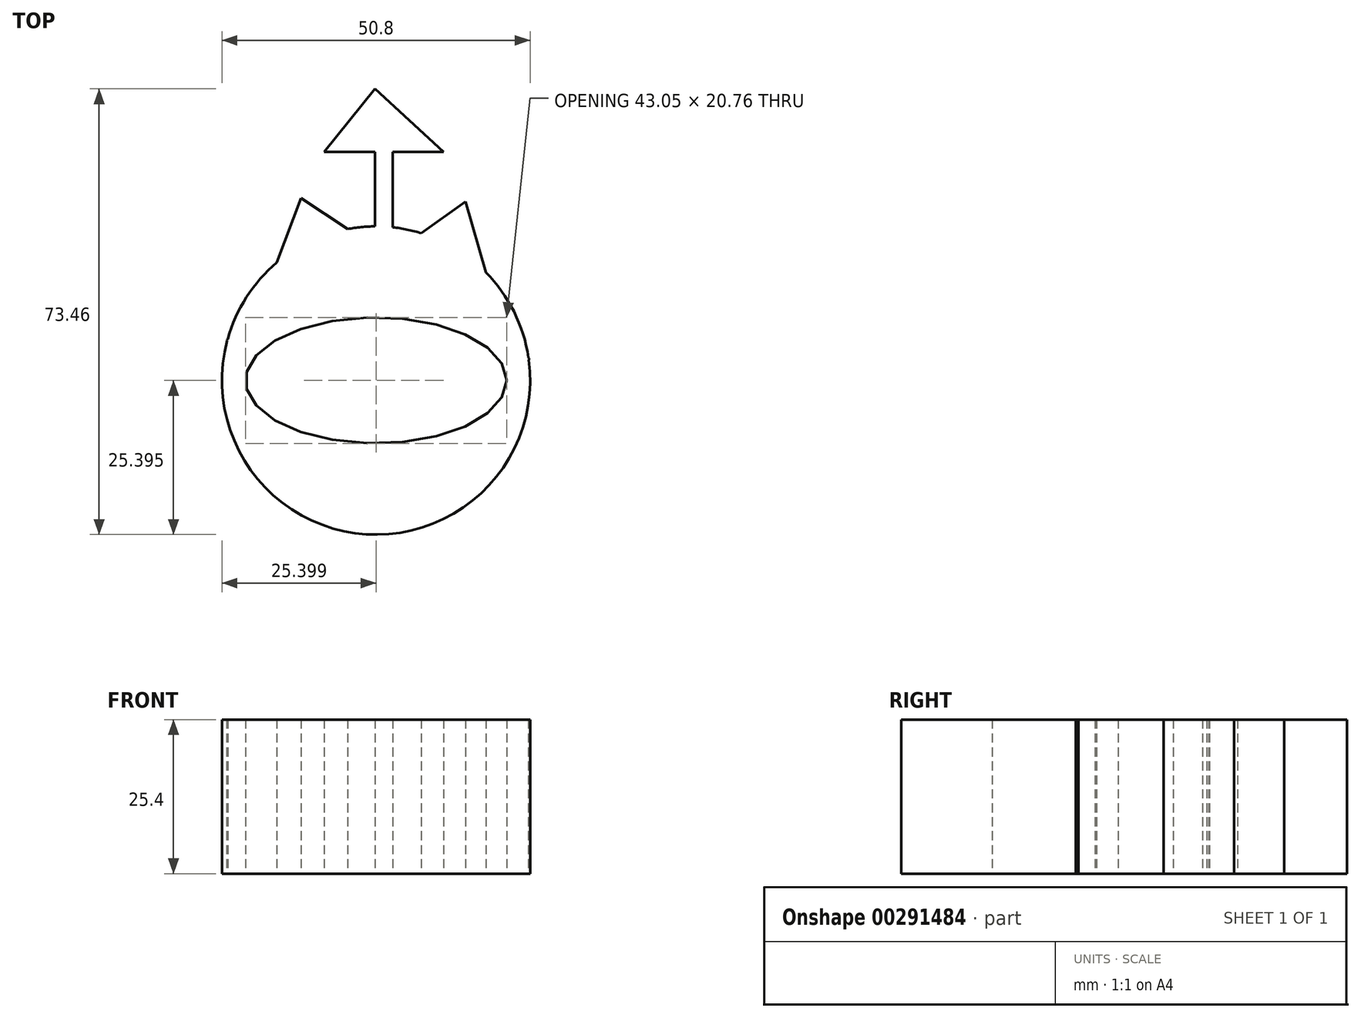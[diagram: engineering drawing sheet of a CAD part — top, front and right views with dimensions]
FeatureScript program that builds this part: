
annotation { "Feature Type Name" : "Feature", "Feature Type Description" : "" }
export const myFeature = defineFeature(function(context is Context, id is Id, definition is map)
    precondition{}
    {
        {
            var Q0;
            Q0=qCreatedBy(makeId("Top.planeOp"),FACE);
            var sketch = newSketch(context, id + "F0", { "sketchPlane" : qUnion([Q0])});
            skArc(sketch, "E0", {"start": v(-48.95, 34.93) * mm, "mid": v(-33.79, -9.89) * mm, "end": v(-14.51, 33.32) * mm});
            skLineSegment(sketch, "E1", {"start": v(-48.95, 34.93) * mm, "end": v(-44.98, 45.53) * mm});
            skLineSegment(sketch, "E2", {"start": v(-37.3, 40.45) * mm, "end": v(-44.98, 45.53) * mm});
            skLineSegment(sketch, "E3", {"start": v(-25.13, 39.76) * mm, "end": v(-17.83, 44.96) * mm});
            skLineSegment(sketch, "E4", {"start": v(-17.83, 44.96) * mm, "end": v(-14.51, 33.32) * mm});
            skLineSegment(sketch, "E5", {"start": v(-32.76, 40.88) * mm, "end": v(-32.76, 53.19) * mm});
            skPoint(sketch, "E6.endSnap0", {"position": v(-21.48, 42.36) * mm});
            skArc(sketch, "E7.trimOffspring", {"start": v(-25.13, 39.76) * mm, "mid": v(-27.48, 40.36) * mm, "end": v(-29.87, 40.74) * mm});
            skFitSpline(sketch, "E8", {"points": [v(-57.14, 22.05) * mm, v(-55.17, 16.3) * mm, v(-50.3, 13.87) * mm, v(-46.63, 12.95) * mm, v(-41.76, 12.95) * mm, v(-41.76, 13.26) * mm, v(-37.19, 12.34) * mm, v(-29.87, 12.34) * mm, v(-27.43, 12.04) * mm, v(-22.86, 12.34) * mm, v(-19.2, 12.95) * mm, v(-9.75, 15.4) * mm, v(-9.75, 15.7) * mm, v(-7.38, 18.94) * mm], "startDerivative": vector(33.63, -64.55) * mm, "endDerivative": vector(45.46, 52.44) * mm});
            skPoint(sketch, "E9.end.orphan", {"position": v(-32.76, 63.55) * mm});
            skPoint(sketch, "E6.end.orphan", {"position": v(-21.48, 53.19) * mm});
            skLineSegment(sketch, "E10", {"start": v(-29.87, 53.19) * mm, "end": v(-29.87, 40.74) * mm});
            skLineSegment(sketch, "E11", {"start": v(-29.87, 53.19) * mm, "end": v(-21.48, 53.19) * mm});
            skLineSegment(sketch, "E12", {"start": v(-32.76, 53.19) * mm, "end": v(-41.14, 53.19) * mm});
            skPoint(sketch, "E12.endSnap0", {"position": v(-41.14, 42.99) * mm});
            skLineSegment(sketch, "E13", {"start": v(-21.48, 53.19) * mm, "end": v(-32.76, 63.55) * mm});
            skLineSegment(sketch, "E14", {"start": v(-41.14, 53.19) * mm, "end": v(-32.76, 63.55) * mm});
            skLineSegment(sketch, "E15", {"start": v(-57.07, 22.31) * mm, "end": v(-57.23, 22.17) * mm});
            skLineSegment(sketch, "E16", {"start": v(-57.14, 22.05) * mm, "end": v(-57.23, 22.17) * mm});
            skLineSegment(sketch, "E17", {"start": v(-7.48, 19.27) * mm, "end": v(-7.36, 19.11) * mm});
            skLineSegment(sketch, "E18", {"start": v(-7.38, 18.94) * mm, "end": v(-7.36, 19.11) * mm});
            skArc(sketch, "E19.trimOffspring", {"start": v(-32.76, 40.88) * mm, "mid": v(-35.04, 40.77) * mm, "end": v(-37.3, 40.45) * mm});
            skPoint(sketch, "E20.2.internal.orphan", {"position": v(-55.17, 22.7) * mm});
            skEllipse(sketch, "E21", {"center": v(-32.6, 15.49) * mm, "majorRadius": 21.53 * mm, "minorRadius": 10.38 * mm, "majorAxis": v(1, 0)});
            skSolve(sketch);
        }
        {
            var Q0;
            Q0 = qSketchRegion(id + "F0", true);
            extrude(context, id + "F1", {"entities" : qUnion([Q0]), "depth" : 25.4 * mm});
        }
    });
